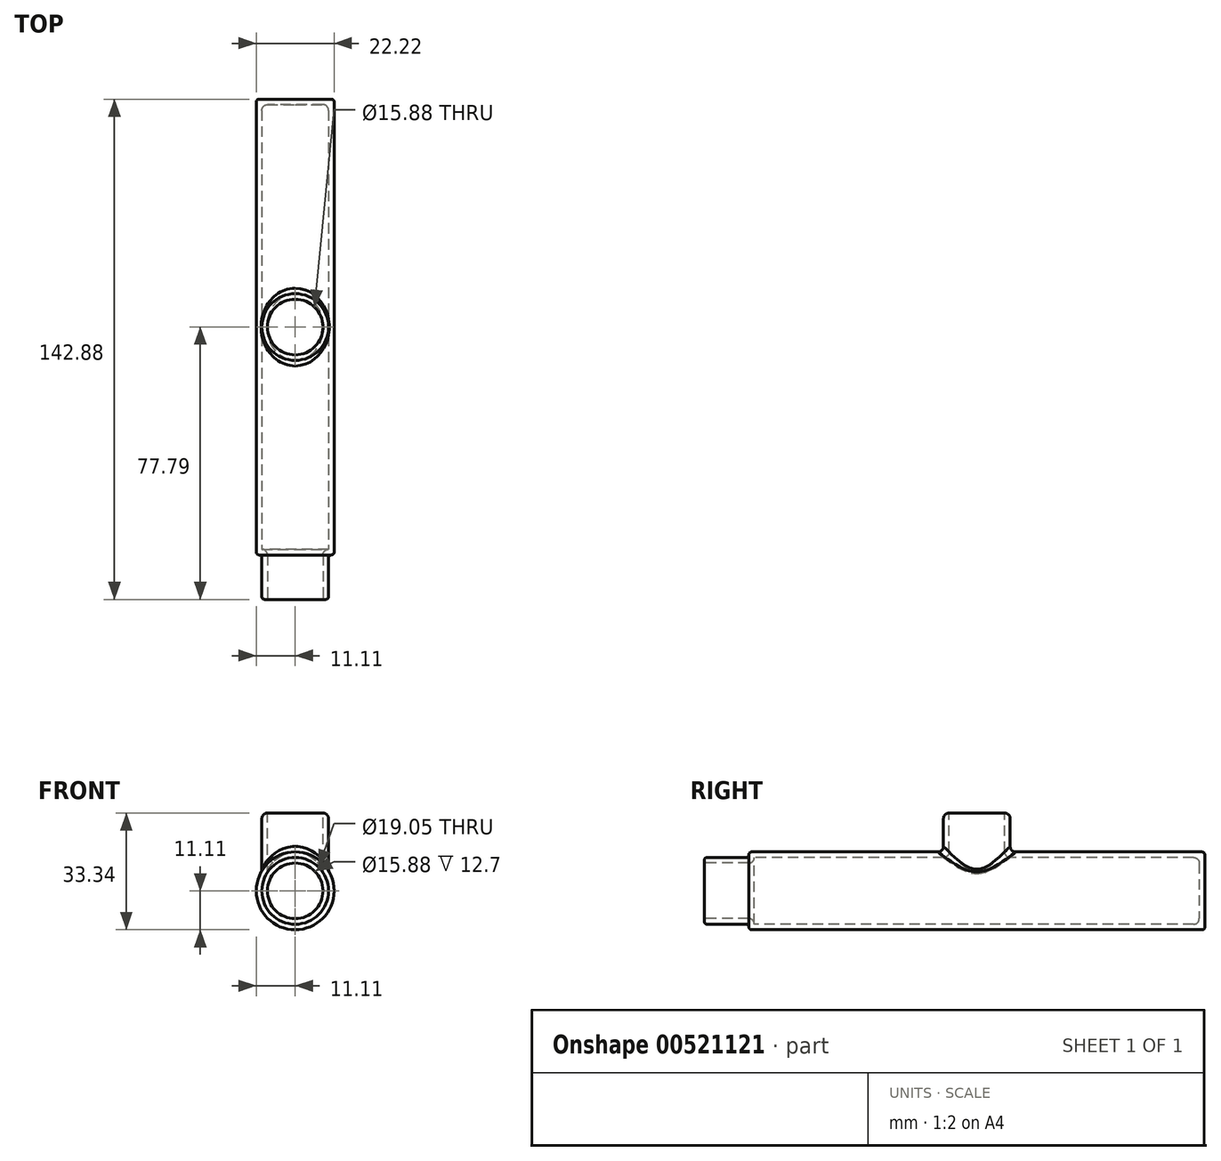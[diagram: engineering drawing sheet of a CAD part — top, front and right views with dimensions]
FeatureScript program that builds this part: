
annotation { "Feature Type Name" : "Feature", "Feature Type Description" : "" }
export const myFeature = defineFeature(function(context is Context, id is Id, definition is map)
    precondition{}
    {
        {
            var Q0;
            Q0=qCreatedBy(makeId("Right.planeOp"),FACE);
            var sketch = newSketch(context, id + "F0", { "sketchPlane" : qUnion([Q0])});
            skLineSegment(sketch, "E0.bottom", {"start": v(-63.5, 11.11) * mm, "end": v(63.5, 11.11) * mm});
            skLineSegment(sketch, "E0.top", {"start": v(-63.5, 9.53) * mm, "end": v(63.5, 9.53) * mm});
            skLineSegment(sketch, "E1.bottom", {"start": v(63.5, 11.11) * mm, "end": v(65.09, 11.11) * mm});
            skLineSegment(sketch, "E1.top", {"start": v(63.5, 0) * mm, "end": v(65.09, 0) * mm});
            skLineSegment(sketch, "E1.left", {"start": v(63.5, 9.53) * mm, "end": v(63.5, 0) * mm});
            skLineSegment(sketch, "E1.right", {"start": v(65.09, 11.11) * mm, "end": v(65.09, 0) * mm});
            skLineSegment(sketch, "E2.bottom", {"start": v(-63.5, 11.11) * mm, "end": v(-65.09, 11.11) * mm});
            skLineSegment(sketch, "E2.top", {"start": v(-63.5, 7.94) * mm, "end": v(-65.09, 7.94) * mm});
            skLineSegment(sketch, "E2.left", {"start": v(-63.5, 9.52) * mm, "end": v(-63.5, 7.94) * mm});
            skLineSegment(sketch, "E2.right", {"start": v(-65.09, 11.11) * mm, "end": v(-65.09, 9.53) * mm});
            skLineSegment(sketch, "E3.bottom", {"start": v(-65.09, 7.94) * mm, "end": v(-77.79, 7.94) * mm});
            skLineSegment(sketch, "E3.top", {"start": v(-65.09, 9.53) * mm, "end": v(-77.79, 9.53) * mm});
            skLineSegment(sketch, "E3.right", {"start": v(-77.79, 7.94) * mm, "end": v(-77.79, 9.53) * mm});
            skLineSegment(sketch, "E4", {"start": v(0, 0) * mm, "end": v(7.03, 0) * mm, "construction": true});
            skSolve(sketch);
        }
        {
            var Q0;
            Q0=makeQuery(id+"F0.imprint","IMPRINT",FACE,{"disambiguationData":[TD([[makeQuery(id+"F0.imprint","IMPRINT",EDGE,{"derivedFrom":sQuery(id+"F0.wireOp",EDGE,"E0.bottom")}),-1.0]])]});
            var Q1;
            Q1=sQuery(id+"F0.wireOp",EDGE,"E4");
            revolve(context, id + "F1", {"entities" : qUnion([Q0]), "axis" : qUnion([Q1]), "revolveType" : RevolveType.FULL});
        }
        {
            var Q0;
            Q0=makeQuery(id+"F1.opRevolve","SWEPT_EDGE",EDGE,{"disambiguationData":[OSD([sQuery(id+"F0.wireOp",EDGE,"E3.top"),sQuery(id+"F0.wireOp",EDGE,"E3.right")])]});
            var Q1;
            Q1=makeQuery(id+"F1.opRevolve","SWEPT_EDGE",EDGE,{"disambiguationData":[OSD([sQuery(id+"F0.wireOp",EDGE,"E2.bottom"),sQuery(id+"F0.wireOp",EDGE,"E2.right")])]});
            var Q2;
            Q2=makeQuery(id+"F1.opRevolve","SWEPT_EDGE",EDGE,{"disambiguationData":[OSD([sQuery(id+"F0.wireOp",EDGE,"E1.bottom"),sQuery(id+"F0.wireOp",EDGE,"E1.right")])]});
            var Q3;
            Q3=makeQuery(id+"F1.opRevolve","SWEPT_EDGE",EDGE,{"disambiguationData":[OSD([sQuery(id+"F0.wireOp",EDGE,"E2.right"),sQuery(id+"F0.wireOp",EDGE,"E3.top")])]});
            fillet(context, id + "F2", {"entities" : qUnion([Q0, Q1, Q2, Q3]), "radius" : 0.8 * mm, "tangentPropagation" : true, "allowEdgeOverflow" : false});
        }
        {
            var Q0;
            Q0=makeQuery(id+"F1.opRevolve","SWEPT_EDGE",EDGE,{"disambiguationData":[OSD([sQuery(id+"F0.wireOp",EDGE,"E2.top"),sQuery(id+"F0.wireOp",EDGE,"E2.left")])]});
            fillet(context, id + "F3", {"entities" : qUnion([Q0]), "radius" : 1.59 * mm, "tangentPropagation" : true, "allowEdgeOverflow" : false});
        }
        {
            var Q0;
            Q0=makeQuery(id+"F1.opRevolve","SWEPT_EDGE",EDGE,{"disambiguationData":[OSD([sQuery(id+"F0.wireOp",EDGE,"E0.top"),sQuery(id+"F0.wireOp",EDGE,"E1.left")])]});
            fillet(context, id + "F4", {"entities" : qUnion([Q0]), "radius" : 1.59 * mm, "tangentPropagation" : true, "allowEdgeOverflow" : false});
        }
        {
            var Q0;
            Q0=qCreatedBy(makeId("Top.planeOp"),FACE);
            var sketch = newSketch(context, id + "F5", { "sketchPlane" : qUnion([Q0])});
            skCircle(sketch, "E5", {"center": v(0, 0) * mm, "radius": 9.53 * mm});
            skSolve(sketch);
        }
        {
            var Q0;
            Q0 = qSketchRegion(id + "F5", true);
            extrude(context, id + "F6", {"entities" : qUnion([Q0]), "operationType" : NewBodyOperationType.ADD, "depth" : 22.22 * mm, "offsetDistance" : 25.4 * mm, "hasSecondDirection" : true, "secondDirectionOppositeDirection" : true, "secondDirectionDepth" : 0 * mm});
        }
        {
            var Q0;
            Q0=qCreatedBy(makeId("Front.planeOp"),FACE);
            var sketch = newSketch(context, id + "F7", { "sketchPlane" : qUnion([Q0])});
            skCircle(sketch, "E6", {"center": v(0, 0) * mm, "radius": 9.53 * mm});
            skSolve(sketch);
        }
        {
            var Q0;
            Q0 = qSketchRegion(id + "F7", true);
            extrude(context, id + "F8", {"entities" : qUnion([Q0]), "operationType" : NewBodyOperationType.REMOVE, "oppositeDirection" : true, "depth" : 25.4 * mm, "offsetDistance" : 25.4 * mm, "hasSecondDirection" : true, "secondDirectionOppositeDirection" : false, "secondDirectionDepth" : 25.4 * mm});
        }
        {
            var Q0;
            Q0=makeQuery(id+"F6.opExtrude","CAP_FACE",FACE,{"disambiguationData":[OSD([sQuery(id+"F5.wireOp",EDGE,"E5")])],"isStart":false});
            var sketch = newSketch(context, id + "F9", { "sketchPlane" : qUnion([Q0])});
            skCircle(sketch, "E7", {"center": v(0, 0) * mm, "radius": 7.94 * mm});
            skSolve(sketch);
        }
        {
            var Q0;
            Q0 = qSketchRegion(id + "F9", true);
            extrude(context, id + "F10", {"entities" : qUnion([Q0]), "operationType" : NewBodyOperationType.REMOVE, "oppositeDirection" : true, "depth" : 25.4 * mm, "offsetDistance" : 25.4 * mm});
        }
        {
            var Q0;
            Q0=makeQuery(id+"F6.boolean.opBoolean","INTERSECT",EDGE,{"derivedFrom":[makeQuery(id+"F1.opRevolve","SWEPT_FACE",FACE,{"disambiguationData":[OSD([sQuery(id+"F0.wireOp",EDGE,"E0.bottom"),sQuery(id+"F0.wireOp",EDGE,"E1.bottom"),sQuery(id+"F0.wireOp",EDGE,"E2.bottom")])]}),makeQuery(id+"F6.opExtrude","SWEPT_FACE",FACE,{"disambiguationData":[OSD([sQuery(id+"F5.wireOp",EDGE,"E5")])]})]});
            var Q1;
            Q1=makeQuery(id+"F6.opExtrude","CAP_EDGE",EDGE,{"disambiguationData":[OSD([sQuery(id+"F5.wireOp",EDGE,"E5")])],"isStart":false});
            var Q2;
            {var subQ0=sQuery(id+"F5.wireOp",EDGE,"E5");Q2=makeQuery(id+"F6.boolean.opBoolean","SPLIT",FACE,{"disambiguationData":[TD([makeQuery(id+"F1.opRevolve","SWEPT_FACE",FACE,{"disambiguationData":[OSD([sQuery(id+"F0.wireOp",EDGE,"E0.bottom"),sQuery(id+"F0.wireOp",EDGE,"E1.bottom"),sQuery(id+"F0.wireOp",EDGE,"E2.bottom")])]}),makeQuery(id+"F6.opExtrude","CAP_FACE",FACE,{"disambiguationData":[OSD([subQ0])],"isStart":true}),makeQuery(id+"F6.opExtrude","CAP_FACE",FACE,{"disambiguationData":[OSD([subQ0])],"isStart":false})])],"derivedFrom":makeQuery(id+"F6.opExtrude","SWEPT_FACE",FACE,{"disambiguationData":[OSD([subQ0])]})});}
            fillet(context, id + "F11", {"entities" : qUnion([Q0, Q1, Q2]), "radius" : 1.59 * mm, "tangentPropagation" : true, "allowEdgeOverflow" : false});
        }
        {
            var Q0;
            Q0=makeQuery(id+"F10.boolean.opBoolean","INTERSECT",EDGE,{"derivedFrom":[makeQuery(id+"F8.boolean.opBoolean","MERGE",FACE,{"derivedFrom":[makeQuery(id+"F1.opRevolve","SWEPT_FACE",FACE,{"disambiguationData":[OSD([sQuery(id+"F0.wireOp",EDGE,"E0.top")])]}),makeQuery(id+"F8.opExtrude","SWEPT_FACE",FACE,{"disambiguationData":[OSD([sQuery(id+"F7.wireOp",EDGE,"E6")])]})]}),makeQuery(id+"F10.opExtrude","SWEPT_FACE",FACE,{"disambiguationData":[OSD([sQuery(id+"F9.wireOp",EDGE,"E7")])]})]});
            fillet(context, id + "F12", {"entities" : qUnion([Q0]), "radius" : 1.59 * mm, "tangentPropagation" : true, "allowEdgeOverflow" : false});
        }
    });
